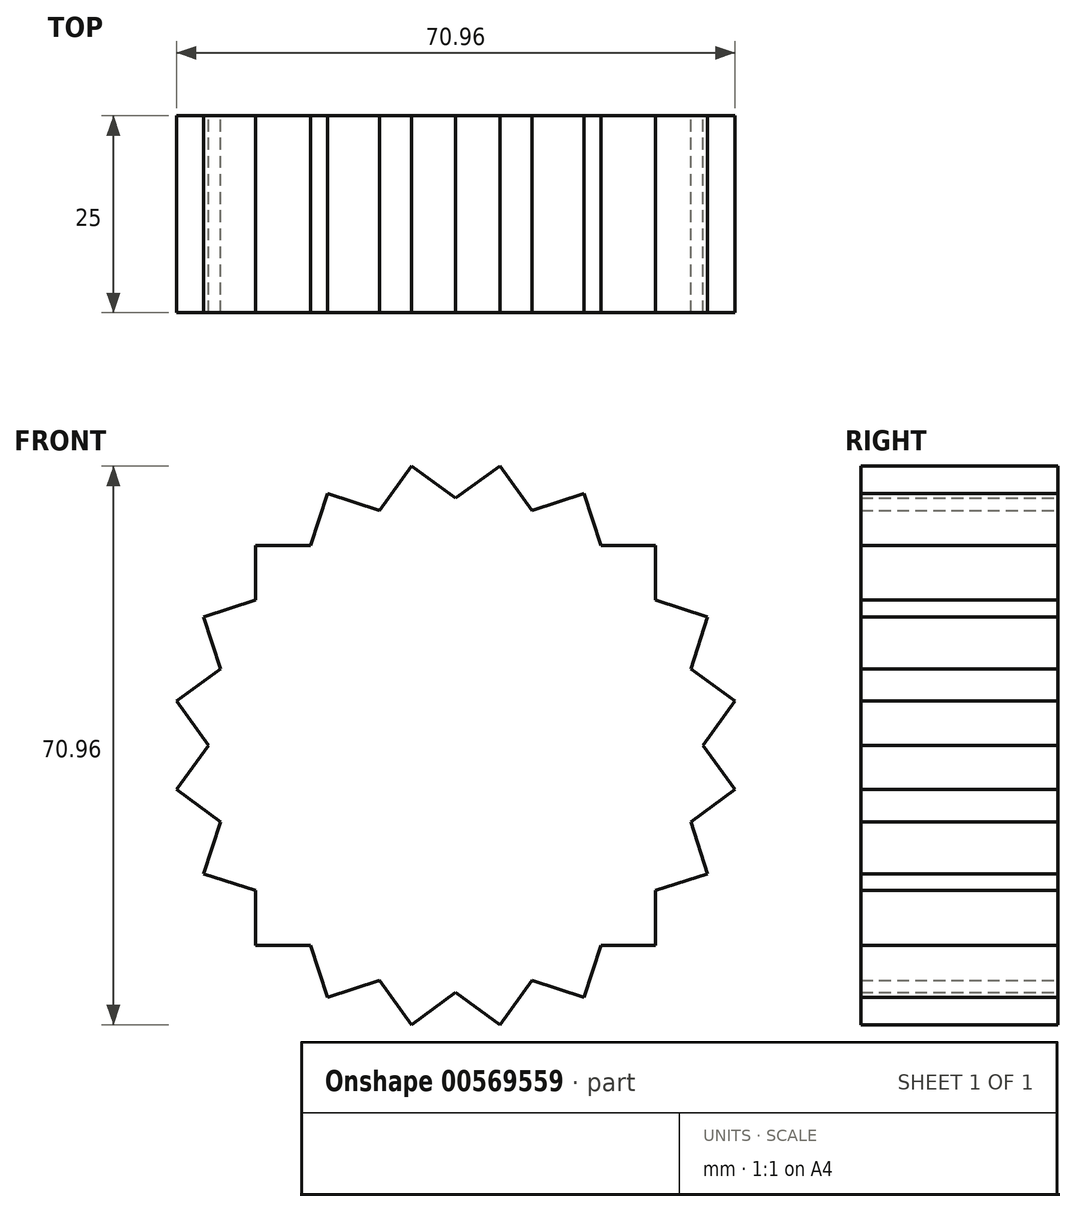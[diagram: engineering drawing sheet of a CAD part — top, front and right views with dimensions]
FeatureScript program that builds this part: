
annotation { "Feature Type Name" : "Feature", "Feature Type Description" : "" }
export const myFeature = defineFeature(function(context is Context, id is Id, definition is map)
    precondition{}
    {
        {
            var Q0;
            Q0=qCreatedBy(makeId("Front.planeOp"),FACE);
            var sketch = newSketch(context, id + "F0", { "sketchPlane" : qUnion([Q0])});
            skLineSegment(sketch, "E0.bottom", {"start": v(-25.4, 25.4) * mm, "end": v(25.4, 25.4) * mm});
            skLineSegment(sketch, "E0.top", {"start": v(-25.4, -25.4) * mm, "end": v(25.4, -25.4) * mm});
            skLineSegment(sketch, "E0.left", {"start": v(-25.4, 25.4) * mm, "end": v(-25.4, -25.4) * mm});
            skLineSegment(sketch, "E0.right", {"start": v(25.4, 25.4) * mm, "end": v(25.4, -25.4) * mm});
            skPoint(sketch, "E0.middle", {"position": v(0, 0) * mm});
            skLineSegment(sketch, "E1.1.0", {"start": v(16.3, -32) * mm, "end": v(32, 16.3) * mm});
            skLineSegment(sketch, "E1.1.1", {"start": v(-32, -16.3) * mm, "end": v(16.3, -32) * mm});
            skLineSegment(sketch, "E1.1.2", {"start": v(-32, -16.3) * mm, "end": v(-16.3, 32) * mm});
            skLineSegment(sketch, "E1.1.3", {"start": v(-16.3, 32) * mm, "end": v(32, 16.3) * mm});
            skLineSegment(sketch, "E1.2.0", {"start": v(35.48, 5.62) * mm, "end": v(-5.62, 35.48) * mm});
            skLineSegment(sketch, "E1.2.1", {"start": v(5.62, -35.48) * mm, "end": v(35.48, 5.62) * mm});
            skLineSegment(sketch, "E1.2.2", {"start": v(5.62, -35.48) * mm, "end": v(-35.48, -5.62) * mm});
            skLineSegment(sketch, "E1.2.3", {"start": v(-35.48, -5.62) * mm, "end": v(-5.62, 35.48) * mm});
            skLineSegment(sketch, "E1.3.0", {"start": v(5.62, 35.48) * mm, "end": v(-35.48, 5.62) * mm});
            skLineSegment(sketch, "E1.3.1", {"start": v(35.48, -5.62) * mm, "end": v(5.62, 35.48) * mm});
            skLineSegment(sketch, "E1.3.2", {"start": v(35.48, -5.62) * mm, "end": v(-5.62, -35.48) * mm});
            skLineSegment(sketch, "E1.3.3", {"start": v(-5.62, -35.48) * mm, "end": v(-35.48, 5.62) * mm});
            skLineSegment(sketch, "E1.4.0", {"start": v(-32, 16.3) * mm, "end": v(-16.3, -32) * mm});
            skLineSegment(sketch, "E1.4.1", {"start": v(16.3, 32) * mm, "end": v(-32, 16.3) * mm});
            skLineSegment(sketch, "E1.4.2", {"start": v(16.3, 32) * mm, "end": v(32, -16.3) * mm});
            skLineSegment(sketch, "E1.4.3", {"start": v(32, -16.3) * mm, "end": v(-16.3, -32) * mm});
            skSolve(sketch);
        }
        {
            var Q0;
            {var subQ0=sQuery(id+"F0.wireOp",EDGE,"E1.2.1");var subQ1=sQuery(id+"F0.wireOp",EDGE,"E1.1.1");var subQ2=makeQuery(id+"F0.imprint","INTERSECT",VERTEX,{"derivedFrom":[subQ1,subQ0]});Q0=makeQuery(id+"F0.imprint","IMPRINT",FACE,{"disambiguationData":[TD([[makeQuery(id+"F0.imprint","IMPRINT",EDGE,{"disambiguationData":[TD([[subQ2,1.0]])],"derivedFrom":subQ1}),-1.0]])]});}
            var Q1;
            {var subQ0=sQuery(id+"F0.wireOp",EDGE,"E1.3.0");var subQ1=sQuery(id+"F0.wireOp",EDGE,"E1.2.0");var subQ2=makeQuery(id+"F0.imprint","INTERSECT",VERTEX,{"derivedFrom":[subQ1,subQ0]});Q1=makeQuery(id+"F0.imprint","IMPRINT",FACE,{"disambiguationData":[TD([[makeQuery(id+"F0.imprint","IMPRINT",EDGE,{"disambiguationData":[TD([[subQ2,1.0]])],"derivedFrom":subQ1}),-1.0]])]});}
            var Q2;
            {var subQ0=sQuery(id+"F0.wireOp",EDGE,"E1.2.2");var subQ1=sQuery(id+"F0.wireOp",EDGE,"E1.1.2");var subQ2=makeQuery(id+"F0.imprint","INTERSECT",VERTEX,{"derivedFrom":[subQ1,subQ0]});Q2=makeQuery(id+"F0.imprint","IMPRINT",FACE,{"disambiguationData":[TD([[makeQuery(id+"F0.imprint","IMPRINT",EDGE,{"disambiguationData":[TD([[subQ2,-1.0]])],"derivedFrom":subQ1}),1.0]])]});}
            var Q3;
            {var subQ10=sQuery(id+"F0.wireOp",EDGE,"E0.bottom");var subQ24=sQuery(id+"F0.wireOp",EDGE,"E1.4.1");var subQ25=makeQuery(id+"F0.imprint","INTERSECT",VERTEX,{"derivedFrom":[subQ10,subQ24]});Q3=makeQuery(id+"F0.imprint","IMPRINT",FACE,{"disambiguationData":[TD([[makeQuery(id+"F0.imprint","IMPRINT",EDGE,{"disambiguationData":[TD([[subQ25,-1.0]])],"derivedFrom":subQ10}),-1.0]])]});}
            var Q4;
            {var subQ0=sQuery(id+"F0.wireOp",EDGE,"E1.1.3");var subQ1=sQuery(id+"F0.wireOp",EDGE,"E0.right");var subQ2=makeQuery(id+"F0.imprint","INTERSECT",VERTEX,{"derivedFrom":[subQ1,subQ0]});Q4=makeQuery(id+"F0.imprint","IMPRINT",FACE,{"disambiguationData":[TD([[makeQuery(id+"F0.imprint","IMPRINT",EDGE,{"disambiguationData":[TD([[subQ2,-1.0]])],"derivedFrom":subQ1}),-1.0]])]});}
            var Q5;
            {var subQ0=sQuery(id+"F0.wireOp",EDGE,"E1.4.0");var subQ1=sQuery(id+"F0.wireOp",EDGE,"E0.top");var subQ2=makeQuery(id+"F0.imprint","INTERSECT",VERTEX,{"derivedFrom":[subQ1,subQ0]});Q5=makeQuery(id+"F0.imprint","IMPRINT",FACE,{"disambiguationData":[TD([[makeQuery(id+"F0.imprint","IMPRINT",EDGE,{"disambiguationData":[TD([[subQ2,-1.0]])],"derivedFrom":subQ1}),1.0]])]});}
            var Q6;
            {var subQ0=sQuery(id+"F0.wireOp",EDGE,"E0.left");var subQ1=sQuery(id+"F0.wireOp",EDGE,"E0.bottom");var subQ2=makeQuery(id+"F0.imprint","INTERSECT",VERTEX,{"derivedFrom":[subQ1,subQ0]});Q6=makeQuery(id+"F0.imprint","IMPRINT",FACE,{"disambiguationData":[TD([[makeQuery(id+"F0.imprint","IMPRINT",EDGE,{"disambiguationData":[TD([[subQ2,-1.0]])],"derivedFrom":subQ1}),-1.0]])]});}
            var Q7;
            {var subQ0=sQuery(id+"F0.wireOp",EDGE,"E1.1.2");var subQ1=sQuery(id+"F0.wireOp",EDGE,"E0.bottom");var subQ2=makeQuery(id+"F0.imprint","INTERSECT",VERTEX,{"derivedFrom":[subQ1,subQ0]});Q7=makeQuery(id+"F0.imprint","IMPRINT",FACE,{"disambiguationData":[TD([[makeQuery(id+"F0.imprint","IMPRINT",EDGE,{"disambiguationData":[TD([[subQ2,-1.0]])],"derivedFrom":subQ1}),1.0]])]});}
            var Q8;
            {var subQ0=sQuery(id+"F0.wireOp",EDGE,"E1.4.2");var subQ1=sQuery(id+"F0.wireOp",EDGE,"E0.bottom");var subQ2=makeQuery(id+"F0.imprint","INTERSECT",VERTEX,{"derivedFrom":[subQ1,subQ0]});Q8=makeQuery(id+"F0.imprint","IMPRINT",FACE,{"disambiguationData":[TD([[makeQuery(id+"F0.imprint","IMPRINT",EDGE,{"disambiguationData":[TD([[subQ2,1.0]])],"derivedFrom":subQ1}),1.0]])]});}
            var Q9;
            {var subQ0=sQuery(id+"F0.wireOp",EDGE,"E0.right");var subQ1=sQuery(id+"F0.wireOp",EDGE,"E0.top");var subQ2=makeQuery(id+"F0.imprint","INTERSECT",VERTEX,{"derivedFrom":[subQ1,subQ0]});Q9=makeQuery(id+"F0.imprint","IMPRINT",FACE,{"disambiguationData":[TD([[makeQuery(id+"F0.imprint","IMPRINT",EDGE,{"disambiguationData":[TD([[subQ2,1.0]])],"derivedFrom":subQ1}),1.0]])]});}
            var Q10;
            {var subQ0=sQuery(id+"F0.wireOp",EDGE,"E1.4.1");var subQ1=sQuery(id+"F0.wireOp",EDGE,"E0.left");var subQ2=makeQuery(id+"F0.imprint","INTERSECT",VERTEX,{"derivedFrom":[subQ1,subQ0]});Q10=makeQuery(id+"F0.imprint","IMPRINT",FACE,{"disambiguationData":[TD([[makeQuery(id+"F0.imprint","IMPRINT",EDGE,{"disambiguationData":[TD([[subQ2,-1.0]])],"derivedFrom":subQ1}),-1.0]])]});}
            var Q11;
            {var subQ0=sQuery(id+"F0.wireOp",EDGE,"E1.1.3");var subQ1=sQuery(id+"F0.wireOp",EDGE,"E0.right");var subQ2=makeQuery(id+"F0.imprint","INTERSECT",VERTEX,{"derivedFrom":[subQ1,subQ0]});Q11=makeQuery(id+"F0.imprint","IMPRINT",FACE,{"disambiguationData":[TD([[makeQuery(id+"F0.imprint","IMPRINT",EDGE,{"disambiguationData":[TD([[subQ2,-1.0]])],"derivedFrom":subQ1}),1.0]])]});}
            var Q12;
            {var subQ0=sQuery(id+"F0.wireOp",EDGE,"E1.4.3");var subQ1=sQuery(id+"F0.wireOp",EDGE,"E0.right");var subQ2=makeQuery(id+"F0.imprint","INTERSECT",VERTEX,{"derivedFrom":[subQ1,subQ0]});Q12=makeQuery(id+"F0.imprint","IMPRINT",FACE,{"disambiguationData":[TD([[makeQuery(id+"F0.imprint","IMPRINT",EDGE,{"disambiguationData":[TD([[subQ2,1.0]])],"derivedFrom":subQ1}),1.0]])]});}
            var Q13;
            {var subQ0=sQuery(id+"F0.wireOp",EDGE,"E1.2.0");var subQ1=sQuery(id+"F0.wireOp",EDGE,"E1.1.0");var subQ2=makeQuery(id+"F0.imprint","INTERSECT",VERTEX,{"derivedFrom":[subQ1,subQ0]});Q13=makeQuery(id+"F0.imprint","IMPRINT",FACE,{"disambiguationData":[TD([[makeQuery(id+"F0.imprint","IMPRINT",EDGE,{"disambiguationData":[TD([[subQ2,1.0]])],"derivedFrom":subQ1}),-1.0]])]});}
            var Q14;
            {var subQ0=sQuery(id+"F0.wireOp",EDGE,"E1.2.3");var subQ1=sQuery(id+"F0.wireOp",EDGE,"E0.left");var subQ2=makeQuery(id+"F0.imprint","INTERSECT",VERTEX,{"derivedFrom":[subQ1,subQ0]});Q14=makeQuery(id+"F0.imprint","IMPRINT",FACE,{"disambiguationData":[TD([[makeQuery(id+"F0.imprint","IMPRINT",EDGE,{"disambiguationData":[TD([[subQ2,-1.0]])],"derivedFrom":subQ1}),-1.0]])]});}
            var Q15;
            {var subQ0=sQuery(id+"F0.wireOp",EDGE,"E1.3.0");var subQ1=sQuery(id+"F0.wireOp",EDGE,"E0.bottom");var subQ2=makeQuery(id+"F0.imprint","INTERSECT",VERTEX,{"derivedFrom":[subQ1,subQ0]});Q15=makeQuery(id+"F0.imprint","IMPRINT",FACE,{"disambiguationData":[TD([[makeQuery(id+"F0.imprint","IMPRINT",EDGE,{"disambiguationData":[TD([[subQ2,-1.0]])],"derivedFrom":subQ1}),1.0]])]});}
            var Q16;
            {var subQ0=sQuery(id+"F0.wireOp",EDGE,"E1.4.3");var subQ1=sQuery(id+"F0.wireOp",EDGE,"E1.1.1");var subQ2=makeQuery(id+"F0.imprint","INTERSECT",VERTEX,{"derivedFrom":[subQ1,subQ0]});Q16=makeQuery(id+"F0.imprint","IMPRINT",FACE,{"disambiguationData":[TD([[makeQuery(id+"F0.imprint","IMPRINT",EDGE,{"disambiguationData":[TD([[subQ2,-1.0]])],"derivedFrom":subQ1}),-1.0]])]});}
            var Q17;
            {var subQ0=sQuery(id+"F0.wireOp",EDGE,"E1.1.0");var subQ1=sQuery(id+"F0.wireOp",EDGE,"E0.top");var subQ2=makeQuery(id+"F0.imprint","INTERSECT",VERTEX,{"derivedFrom":[subQ1,subQ0]});Q17=makeQuery(id+"F0.imprint","IMPRINT",FACE,{"disambiguationData":[TD([[makeQuery(id+"F0.imprint","IMPRINT",EDGE,{"disambiguationData":[TD([[subQ2,1.0]])],"derivedFrom":subQ1}),1.0]])]});}
            var Q18;
            {var subQ0=sQuery(id+"F0.wireOp",EDGE,"E1.3.0");var subQ1=sQuery(id+"F0.wireOp",EDGE,"E1.1.3");var subQ2=makeQuery(id+"F0.imprint","INTERSECT",VERTEX,{"derivedFrom":[subQ1,subQ0]});Q18=makeQuery(id+"F0.imprint","IMPRINT",FACE,{"disambiguationData":[TD([[makeQuery(id+"F0.imprint","IMPRINT",EDGE,{"disambiguationData":[TD([[subQ2,-1.0]])],"derivedFrom":subQ1}),1.0]])]});}
            var Q19;
            {var subQ0=sQuery(id+"F0.wireOp",EDGE,"E1.3.3");var subQ1=sQuery(id+"F0.wireOp",EDGE,"E1.2.3");var subQ2=makeQuery(id+"F0.imprint","INTERSECT",VERTEX,{"derivedFrom":[subQ1,subQ0]});Q19=makeQuery(id+"F0.imprint","IMPRINT",FACE,{"disambiguationData":[TD([[makeQuery(id+"F0.imprint","IMPRINT",EDGE,{"disambiguationData":[TD([[subQ2,-1.0]])],"derivedFrom":subQ1}),1.0]])]});}
            var Q20;
            {var subQ0=sQuery(id+"F0.wireOp",EDGE,"E1.3.0");var subQ1=sQuery(id+"F0.wireOp",EDGE,"E1.1.2");var subQ2=makeQuery(id+"F0.imprint","INTERSECT",VERTEX,{"derivedFrom":[subQ1,subQ0]});Q20=makeQuery(id+"F0.imprint","IMPRINT",FACE,{"disambiguationData":[TD([[makeQuery(id+"F0.imprint","IMPRINT",EDGE,{"disambiguationData":[TD([[subQ2,-1.0]])],"derivedFrom":subQ1}),-1.0]])]});}
            var Q21;
            {var subQ0=sQuery(id+"F0.wireOp",EDGE,"E1.3.1");var subQ1=sQuery(id+"F0.wireOp",EDGE,"E0.right");var subQ2=makeQuery(id+"F0.imprint","INTERSECT",VERTEX,{"derivedFrom":[subQ1,subQ0]});Q21=makeQuery(id+"F0.imprint","IMPRINT",FACE,{"disambiguationData":[TD([[makeQuery(id+"F0.imprint","IMPRINT",EDGE,{"disambiguationData":[TD([[subQ2,-1.0]])],"derivedFrom":subQ1}),1.0]])]});}
            var Q22;
            {var subQ0=sQuery(id+"F0.wireOp",EDGE,"E1.2.2");var subQ1=sQuery(id+"F0.wireOp",EDGE,"E0.top");var subQ2=makeQuery(id+"F0.imprint","INTERSECT",VERTEX,{"derivedFrom":[subQ1,subQ0]});Q22=makeQuery(id+"F0.imprint","IMPRINT",FACE,{"disambiguationData":[TD([[makeQuery(id+"F0.imprint","IMPRINT",EDGE,{"disambiguationData":[TD([[subQ2,-1.0]])],"derivedFrom":subQ1}),-1.0]])]});}
            var Q23;
            {var subQ0=sQuery(id+"F0.wireOp",EDGE,"E1.1.0");var subQ1=sQuery(id+"F0.wireOp",EDGE,"E0.right");var subQ2=makeQuery(id+"F0.imprint","INTERSECT",VERTEX,{"derivedFrom":[subQ1,subQ0]});Q23=makeQuery(id+"F0.imprint","IMPRINT",FACE,{"disambiguationData":[TD([[makeQuery(id+"F0.imprint","IMPRINT",EDGE,{"disambiguationData":[TD([[subQ2,-1.0]])],"derivedFrom":subQ1}),1.0]])]});}
            var Q24;
            {var subQ0=sQuery(id+"F0.wireOp",EDGE,"E1.3.3");var subQ1=sQuery(id+"F0.wireOp",EDGE,"E0.left");var subQ2=makeQuery(id+"F0.imprint","INTERSECT",VERTEX,{"derivedFrom":[subQ1,subQ0]});Q24=makeQuery(id+"F0.imprint","IMPRINT",FACE,{"disambiguationData":[TD([[makeQuery(id+"F0.imprint","IMPRINT",EDGE,{"disambiguationData":[TD([[subQ2,-1.0]])],"derivedFrom":subQ1}),-1.0]])]});}
            var Q25;
            {var subQ0=sQuery(id+"F0.wireOp",EDGE,"E1.2.1");var subQ1=sQuery(id+"F0.wireOp",EDGE,"E0.right");var subQ2=makeQuery(id+"F0.imprint","INTERSECT",VERTEX,{"derivedFrom":[subQ1,subQ0]});Q25=makeQuery(id+"F0.imprint","IMPRINT",FACE,{"disambiguationData":[TD([[makeQuery(id+"F0.imprint","IMPRINT",EDGE,{"disambiguationData":[TD([[subQ2,-1.0]])],"derivedFrom":subQ1}),1.0]])]});}
            var Q26;
            {var subQ0=sQuery(id+"F0.wireOp",EDGE,"E1.3.0");var subQ1=sQuery(id+"F0.wireOp",EDGE,"E0.left");var subQ2=makeQuery(id+"F0.imprint","INTERSECT",VERTEX,{"derivedFrom":[subQ1,subQ0]});Q26=makeQuery(id+"F0.imprint","IMPRINT",FACE,{"disambiguationData":[TD([[makeQuery(id+"F0.imprint","IMPRINT",EDGE,{"disambiguationData":[TD([[subQ2,-1.0]])],"derivedFrom":subQ1}),-1.0]])]});}
            var Q27;
            {var subQ0=sQuery(id+"F0.wireOp",EDGE,"E1.3.2");var subQ1=sQuery(id+"F0.wireOp",EDGE,"E0.top");var subQ2=makeQuery(id+"F0.imprint","INTERSECT",VERTEX,{"derivedFrom":[subQ1,subQ0]});Q27=makeQuery(id+"F0.imprint","IMPRINT",FACE,{"disambiguationData":[TD([[makeQuery(id+"F0.imprint","IMPRINT",EDGE,{"disambiguationData":[TD([[subQ2,-1.0]])],"derivedFrom":subQ1}),1.0]])]});}
            var Q28;
            {var subQ0=sQuery(id+"F0.wireOp",EDGE,"E0.right");var subQ1=sQuery(id+"F0.wireOp",EDGE,"E0.bottom");var subQ2=makeQuery(id+"F0.imprint","INTERSECT",VERTEX,{"derivedFrom":[subQ1,subQ0]});Q28=makeQuery(id+"F0.imprint","IMPRINT",FACE,{"disambiguationData":[TD([[makeQuery(id+"F0.imprint","IMPRINT",EDGE,{"disambiguationData":[TD([[subQ2,1.0]])],"derivedFrom":subQ1}),-1.0]])]});}
            var Q29;
            {var subQ0=sQuery(id+"F0.wireOp",EDGE,"E1.2.0");var subQ1=sQuery(id+"F0.wireOp",EDGE,"E0.bottom");var subQ2=makeQuery(id+"F0.imprint","INTERSECT",VERTEX,{"derivedFrom":[subQ1,subQ0]});Q29=makeQuery(id+"F0.imprint","IMPRINT",FACE,{"disambiguationData":[TD([[makeQuery(id+"F0.imprint","IMPRINT",EDGE,{"disambiguationData":[TD([[subQ2,-1.0]])],"derivedFrom":subQ1}),-1.0]])]});}
            var Q30;
            {var subQ0=sQuery(id+"F0.wireOp",EDGE,"E1.4.3");var subQ1=sQuery(id+"F0.wireOp",EDGE,"E0.top");var subQ2=makeQuery(id+"F0.imprint","INTERSECT",VERTEX,{"derivedFrom":[subQ1,subQ0]});Q30=makeQuery(id+"F0.imprint","IMPRINT",FACE,{"disambiguationData":[TD([[makeQuery(id+"F0.imprint","IMPRINT",EDGE,{"disambiguationData":[TD([[subQ2,-1.0]])],"derivedFrom":subQ1}),-1.0]])]});}
            var Q31;
            {var subQ0=sQuery(id+"F0.wireOp",EDGE,"E0.left");var subQ1=sQuery(id+"F0.wireOp",EDGE,"E0.top");var subQ2=makeQuery(id+"F0.imprint","INTERSECT",VERTEX,{"derivedFrom":[subQ1,subQ0]});Q31=makeQuery(id+"F0.imprint","IMPRINT",FACE,{"disambiguationData":[TD([[makeQuery(id+"F0.imprint","IMPRINT",EDGE,{"disambiguationData":[TD([[subQ2,-1.0]])],"derivedFrom":subQ1}),1.0]])]});}
            var Q32;
            {var subQ0=sQuery(id+"F0.wireOp",EDGE,"E1.4.0");var subQ1=sQuery(id+"F0.wireOp",EDGE,"E0.top");var subQ2=makeQuery(id+"F0.imprint","INTERSECT",VERTEX,{"derivedFrom":[subQ1,subQ0]});Q32=makeQuery(id+"F0.imprint","IMPRINT",FACE,{"disambiguationData":[TD([[makeQuery(id+"F0.imprint","IMPRINT",EDGE,{"disambiguationData":[TD([[subQ2,-1.0]])],"derivedFrom":subQ1}),-1.0]])]});}
            var Q33;
            {var subQ0=sQuery(id+"F0.wireOp",EDGE,"E1.1.0");var subQ1=sQuery(id+"F0.wireOp",EDGE,"E0.top");var subQ2=makeQuery(id+"F0.imprint","INTERSECT",VERTEX,{"derivedFrom":[subQ1,subQ0]});Q33=makeQuery(id+"F0.imprint","IMPRINT",FACE,{"disambiguationData":[TD([[makeQuery(id+"F0.imprint","IMPRINT",EDGE,{"disambiguationData":[TD([[subQ2,1.0]])],"derivedFrom":subQ1}),-1.0]])]});}
            var Q34;
            {var subQ0=sQuery(id+"F0.wireOp",EDGE,"E1.1.1");var subQ1=sQuery(id+"F0.wireOp",EDGE,"E0.left");var subQ2=makeQuery(id+"F0.imprint","INTERSECT",VERTEX,{"derivedFrom":[subQ1,subQ0]});Q34=makeQuery(id+"F0.imprint","IMPRINT",FACE,{"disambiguationData":[TD([[makeQuery(id+"F0.imprint","IMPRINT",EDGE,{"disambiguationData":[TD([[subQ2,1.0]])],"derivedFrom":subQ1}),-1.0]])]});}
            var Q35;
            {var subQ0=sQuery(id+"F0.wireOp",EDGE,"E1.4.3");var subQ1=sQuery(id+"F0.wireOp",EDGE,"E0.right");var subQ2=makeQuery(id+"F0.imprint","INTERSECT",VERTEX,{"derivedFrom":[subQ1,subQ0]});Q35=makeQuery(id+"F0.imprint","IMPRINT",FACE,{"disambiguationData":[TD([[makeQuery(id+"F0.imprint","IMPRINT",EDGE,{"disambiguationData":[TD([[subQ2,1.0]])],"derivedFrom":subQ1}),-1.0]])]});}
            var Q36;
            {var subQ0=sQuery(id+"F0.wireOp",EDGE,"E1.2.1");var subQ1=sQuery(id+"F0.wireOp",EDGE,"E0.right");var subQ2=makeQuery(id+"F0.imprint","INTERSECT",VERTEX,{"derivedFrom":[subQ1,subQ0]});Q36=makeQuery(id+"F0.imprint","IMPRINT",FACE,{"disambiguationData":[TD([[makeQuery(id+"F0.imprint","IMPRINT",EDGE,{"disambiguationData":[TD([[subQ2,-1.0]])],"derivedFrom":subQ1}),-1.0]])]});}
            var Q37;
            {var subQ0=sQuery(id+"F0.wireOp",EDGE,"E1.3.3");var subQ1=sQuery(id+"F0.wireOp",EDGE,"E0.left");var subQ2=makeQuery(id+"F0.imprint","INTERSECT",VERTEX,{"derivedFrom":[subQ1,subQ0]});Q37=makeQuery(id+"F0.imprint","IMPRINT",FACE,{"disambiguationData":[TD([[makeQuery(id+"F0.imprint","IMPRINT",EDGE,{"disambiguationData":[TD([[subQ2,-1.0]])],"derivedFrom":subQ1}),1.0]])]});}
            var Q38;
            {var subQ0=sQuery(id+"F0.wireOp",EDGE,"E1.2.3");var subQ1=sQuery(id+"F0.wireOp",EDGE,"E1.1.3");var subQ2=makeQuery(id+"F0.imprint","INTERSECT",VERTEX,{"derivedFrom":[subQ1,subQ0]});Q38=makeQuery(id+"F0.imprint","IMPRINT",FACE,{"disambiguationData":[TD([[makeQuery(id+"F0.imprint","IMPRINT",EDGE,{"disambiguationData":[TD([[subQ2,-1.0]])],"derivedFrom":subQ1}),1.0]])]});}
            var Q39;
            {var subQ0=sQuery(id+"F0.wireOp",EDGE,"E1.3.2");var subQ1=sQuery(id+"F0.wireOp",EDGE,"E0.top");var subQ2=makeQuery(id+"F0.imprint","INTERSECT",VERTEX,{"derivedFrom":[subQ1,subQ0]});Q39=makeQuery(id+"F0.imprint","IMPRINT",FACE,{"disambiguationData":[TD([[makeQuery(id+"F0.imprint","IMPRINT",EDGE,{"disambiguationData":[TD([[subQ2,-1.0]])],"derivedFrom":subQ1}),-1.0]])]});}
            var Q40;
            {var subQ0=sQuery(id+"F0.wireOp",EDGE,"E1.2.0");var subQ1=sQuery(id+"F0.wireOp",EDGE,"E0.bottom");var subQ2=makeQuery(id+"F0.imprint","INTERSECT",VERTEX,{"derivedFrom":[subQ1,subQ0]});Q40=makeQuery(id+"F0.imprint","IMPRINT",FACE,{"disambiguationData":[TD([[makeQuery(id+"F0.imprint","IMPRINT",EDGE,{"disambiguationData":[TD([[subQ2,-1.0]])],"derivedFrom":subQ1}),1.0]])]});}
            var Q41;
            {var subQ0=sQuery(id+"F0.wireOp",EDGE,"E1.4.2");var subQ1=sQuery(id+"F0.wireOp",EDGE,"E0.bottom");var subQ2=makeQuery(id+"F0.imprint","INTERSECT",VERTEX,{"derivedFrom":[subQ1,subQ0]});Q41=makeQuery(id+"F0.imprint","IMPRINT",FACE,{"disambiguationData":[TD([[makeQuery(id+"F0.imprint","IMPRINT",EDGE,{"disambiguationData":[TD([[subQ2,1.0]])],"derivedFrom":subQ1}),-1.0]])]});}
            var Q42;
            {var subQ0=sQuery(id+"F0.wireOp",EDGE,"E1.3.1");var subQ1=sQuery(id+"F0.wireOp",EDGE,"E1.2.1");var subQ2=makeQuery(id+"F0.imprint","INTERSECT",VERTEX,{"derivedFrom":[subQ1,subQ0]});Q42=makeQuery(id+"F0.imprint","IMPRINT",FACE,{"disambiguationData":[TD([[makeQuery(id+"F0.imprint","IMPRINT",EDGE,{"disambiguationData":[TD([[subQ2,1.0]])],"derivedFrom":subQ1}),-1.0]])]});}
            var Q43;
            {var subQ0=sQuery(id+"F0.wireOp",EDGE,"E1.4.2");var subQ1=sQuery(id+"F0.wireOp",EDGE,"E1.1.0");var subQ2=makeQuery(id+"F0.imprint","INTERSECT",VERTEX,{"derivedFrom":[subQ1,subQ0]});Q43=makeQuery(id+"F0.imprint","IMPRINT",FACE,{"disambiguationData":[TD([[makeQuery(id+"F0.imprint","IMPRINT",EDGE,{"disambiguationData":[TD([[subQ2,-1.0]])],"derivedFrom":subQ1}),-1.0]])]});}
            var Q44;
            {var subQ0=sQuery(id+"F0.wireOp",EDGE,"E1.3.1");var subQ1=sQuery(id+"F0.wireOp",EDGE,"E1.1.3");var subQ2=makeQuery(id+"F0.imprint","INTERSECT",VERTEX,{"derivedFrom":[subQ1,subQ0]});Q44=makeQuery(id+"F0.imprint","IMPRINT",FACE,{"disambiguationData":[TD([[makeQuery(id+"F0.imprint","IMPRINT",EDGE,{"disambiguationData":[TD([[subQ2,-1.0]])],"derivedFrom":subQ1}),-1.0]])]});}
            var Q45;
            {var subQ0=sQuery(id+"F0.wireOp",EDGE,"E1.1.1");var subQ1=sQuery(id+"F0.wireOp",EDGE,"E0.left");var subQ2=makeQuery(id+"F0.imprint","INTERSECT",VERTEX,{"derivedFrom":[subQ1,subQ0]});Q45=makeQuery(id+"F0.imprint","IMPRINT",FACE,{"disambiguationData":[TD([[makeQuery(id+"F0.imprint","IMPRINT",EDGE,{"disambiguationData":[TD([[subQ2,1.0]])],"derivedFrom":subQ1}),1.0]])]});}
            var Q46;
            {var subQ0=sQuery(id+"F0.wireOp",EDGE,"E1.3.0");var subQ1=sQuery(id+"F0.wireOp",EDGE,"E0.left");var subQ2=makeQuery(id+"F0.imprint","INTERSECT",VERTEX,{"derivedFrom":[subQ1,subQ0]});Q46=makeQuery(id+"F0.imprint","IMPRINT",FACE,{"disambiguationData":[TD([[makeQuery(id+"F0.imprint","IMPRINT",EDGE,{"disambiguationData":[TD([[subQ2,-1.0]])],"derivedFrom":subQ1}),1.0]])]});}
            var Q47;
            {var subQ0=sQuery(id+"F0.wireOp",EDGE,"E1.2.3");var subQ1=sQuery(id+"F0.wireOp",EDGE,"E0.bottom");var subQ2=makeQuery(id+"F0.imprint","INTERSECT",VERTEX,{"derivedFrom":[subQ1,subQ0]});Q47=makeQuery(id+"F0.imprint","IMPRINT",FACE,{"disambiguationData":[TD([[makeQuery(id+"F0.imprint","IMPRINT",EDGE,{"disambiguationData":[TD([[subQ2,-1.0]])],"derivedFrom":subQ1}),1.0]])]});}
            var Q48;
            {var subQ0=sQuery(id+"F0.wireOp",EDGE,"E1.4.3");var subQ1=sQuery(id+"F0.wireOp",EDGE,"E1.1.0");var subQ2=makeQuery(id+"F0.imprint","INTERSECT",VERTEX,{"derivedFrom":[subQ1,subQ0]});Q48=makeQuery(id+"F0.imprint","IMPRINT",FACE,{"disambiguationData":[TD([[makeQuery(id+"F0.imprint","IMPRINT",EDGE,{"disambiguationData":[TD([[subQ2,-1.0]])],"derivedFrom":subQ1}),1.0]])]});}
            var Q49;
            {var subQ0=sQuery(id+"F0.wireOp",EDGE,"E1.4.1");var subQ1=sQuery(id+"F0.wireOp",EDGE,"E0.left");var subQ2=makeQuery(id+"F0.imprint","INTERSECT",VERTEX,{"derivedFrom":[subQ1,subQ0]});Q49=makeQuery(id+"F0.imprint","IMPRINT",FACE,{"disambiguationData":[TD([[makeQuery(id+"F0.imprint","IMPRINT",EDGE,{"disambiguationData":[TD([[subQ2,-1.0]])],"derivedFrom":subQ1}),1.0]])]});}
            var Q50;
            {var subQ0=sQuery(id+"F0.wireOp",EDGE,"E1.3.3");var subQ1=sQuery(id+"F0.wireOp",EDGE,"E1.1.2");var subQ2=makeQuery(id+"F0.imprint","INTERSECT",VERTEX,{"derivedFrom":[subQ1,subQ0]});Q50=makeQuery(id+"F0.imprint","IMPRINT",FACE,{"disambiguationData":[TD([[makeQuery(id+"F0.imprint","IMPRINT",EDGE,{"disambiguationData":[TD([[subQ2,-1.0]])],"derivedFrom":subQ1}),1.0]])]});}
            var Q51;
            {var subQ0=sQuery(id+"F0.wireOp",EDGE,"E1.2.0");var subQ1=sQuery(id+"F0.wireOp",EDGE,"E0.right");var subQ2=makeQuery(id+"F0.imprint","INTERSECT",VERTEX,{"derivedFrom":[subQ1,subQ0]});Q51=makeQuery(id+"F0.imprint","IMPRINT",FACE,{"disambiguationData":[TD([[makeQuery(id+"F0.imprint","IMPRINT",EDGE,{"disambiguationData":[TD([[subQ2,-1.0]])],"derivedFrom":subQ1}),-1.0]])]});}
            var Q52;
            {var subQ0=sQuery(id+"F0.wireOp",EDGE,"E1.3.3");var subQ1=sQuery(id+"F0.wireOp",EDGE,"E0.top");var subQ2=makeQuery(id+"F0.imprint","INTERSECT",VERTEX,{"derivedFrom":[subQ1,subQ0]});Q52=makeQuery(id+"F0.imprint","IMPRINT",FACE,{"disambiguationData":[TD([[makeQuery(id+"F0.imprint","IMPRINT",EDGE,{"disambiguationData":[TD([[subQ2,-1.0]])],"derivedFrom":subQ1}),-1.0]])]});}
            var Q53;
            {var subQ0=sQuery(id+"F0.wireOp",EDGE,"E1.2.0");var subQ1=sQuery(id+"F0.wireOp",EDGE,"E0.right");var subQ2=makeQuery(id+"F0.imprint","INTERSECT",VERTEX,{"derivedFrom":[subQ1,subQ0]});Q53=makeQuery(id+"F0.imprint","IMPRINT",FACE,{"disambiguationData":[TD([[makeQuery(id+"F0.imprint","IMPRINT",EDGE,{"disambiguationData":[TD([[subQ2,-1.0]])],"derivedFrom":subQ1}),1.0]])]});}
            var Q54;
            {var subQ0=sQuery(id+"F0.wireOp",EDGE,"E1.3.3");var subQ1=sQuery(id+"F0.wireOp",EDGE,"E0.top");var subQ2=makeQuery(id+"F0.imprint","INTERSECT",VERTEX,{"derivedFrom":[subQ1,subQ0]});Q54=makeQuery(id+"F0.imprint","IMPRINT",FACE,{"disambiguationData":[TD([[makeQuery(id+"F0.imprint","IMPRINT",EDGE,{"disambiguationData":[TD([[subQ2,-1.0]])],"derivedFrom":subQ1}),1.0]])]});}
            var Q55;
            {var subQ0=sQuery(id+"F0.wireOp",EDGE,"E1.4.0");var subQ1=sQuery(id+"F0.wireOp",EDGE,"E0.left");var subQ2=makeQuery(id+"F0.imprint","INTERSECT",VERTEX,{"derivedFrom":[subQ1,subQ0]});Q55=makeQuery(id+"F0.imprint","IMPRINT",FACE,{"disambiguationData":[TD([[makeQuery(id+"F0.imprint","IMPRINT",EDGE,{"disambiguationData":[TD([[subQ2,-1.0]])],"derivedFrom":subQ1}),-1.0]])]});}
            var Q56;
            {var subQ0=sQuery(id+"F0.wireOp",EDGE,"E1.1.3");var subQ1=sQuery(id+"F0.wireOp",EDGE,"E0.bottom");var subQ2=makeQuery(id+"F0.imprint","INTERSECT",VERTEX,{"derivedFrom":[subQ1,subQ0]});Q56=makeQuery(id+"F0.imprint","IMPRINT",FACE,{"disambiguationData":[TD([[makeQuery(id+"F0.imprint","IMPRINT",EDGE,{"disambiguationData":[TD([[subQ2,-1.0]])],"derivedFrom":subQ1}),1.0]])]});}
            var Q57;
            {var subQ0=sQuery(id+"F0.wireOp",EDGE,"E1.1.2");var subQ1=sQuery(id+"F0.wireOp",EDGE,"E0.bottom");var subQ2=makeQuery(id+"F0.imprint","INTERSECT",VERTEX,{"derivedFrom":[subQ1,subQ0]});Q57=makeQuery(id+"F0.imprint","IMPRINT",FACE,{"disambiguationData":[TD([[makeQuery(id+"F0.imprint","IMPRINT",EDGE,{"disambiguationData":[TD([[subQ2,-1.0]])],"derivedFrom":subQ1}),-1.0]])]});}
            var Q58;
            {var subQ0=sQuery(id+"F0.wireOp",EDGE,"E1.3.2");var subQ1=sQuery(id+"F0.wireOp",EDGE,"E1.2.2");var subQ2=makeQuery(id+"F0.imprint","INTERSECT",VERTEX,{"derivedFrom":[subQ1,subQ0]});Q58=makeQuery(id+"F0.imprint","IMPRINT",FACE,{"disambiguationData":[TD([[makeQuery(id+"F0.imprint","IMPRINT",EDGE,{"disambiguationData":[TD([[subQ2,-1.0]])],"derivedFrom":subQ1}),1.0]])]});}
            var Q59;
            {var subQ0=sQuery(id+"F0.wireOp",EDGE,"E1.4.0");var subQ1=sQuery(id+"F0.wireOp",EDGE,"E1.1.1");var subQ2=makeQuery(id+"F0.imprint","INTERSECT",VERTEX,{"derivedFrom":[subQ1,subQ0]});Q59=makeQuery(id+"F0.imprint","IMPRINT",FACE,{"disambiguationData":[TD([[makeQuery(id+"F0.imprint","IMPRINT",EDGE,{"disambiguationData":[TD([[subQ2,-1.0]])],"derivedFrom":subQ1}),1.0]])]});}
            var Q60;
            {var subQ0=sQuery(id+"F0.wireOp",EDGE,"E1.2.3");var subQ1=sQuery(id+"F0.wireOp",EDGE,"E0.bottom");var subQ2=makeQuery(id+"F0.imprint","INTERSECT",VERTEX,{"derivedFrom":[subQ1,subQ0]});Q60=makeQuery(id+"F0.imprint","IMPRINT",FACE,{"disambiguationData":[TD([[makeQuery(id+"F0.imprint","IMPRINT",EDGE,{"disambiguationData":[TD([[subQ2,-1.0]])],"derivedFrom":subQ1}),-1.0]])]});}
            var Q61;
            {var subQ0=sQuery(id+"F0.wireOp",EDGE,"E1.3.2");var subQ1=sQuery(id+"F0.wireOp",EDGE,"E1.1.0");var subQ2=makeQuery(id+"F0.imprint","INTERSECT",VERTEX,{"derivedFrom":[subQ1,subQ0]});Q61=makeQuery(id+"F0.imprint","IMPRINT",FACE,{"disambiguationData":[TD([[makeQuery(id+"F0.imprint","IMPRINT",EDGE,{"disambiguationData":[TD([[subQ2,-1.0]])],"derivedFrom":subQ1}),1.0]])]});}
            var Q62;
            {var subQ0=sQuery(id+"F0.wireOp",EDGE,"E1.1.2");var subQ1=sQuery(id+"F0.wireOp",EDGE,"E0.left");var subQ2=makeQuery(id+"F0.imprint","INTERSECT",VERTEX,{"derivedFrom":[subQ1,subQ0]});Q62=makeQuery(id+"F0.imprint","IMPRINT",FACE,{"disambiguationData":[TD([[makeQuery(id+"F0.imprint","IMPRINT",EDGE,{"disambiguationData":[TD([[subQ2,-1.0]])],"derivedFrom":subQ1}),-1.0]])]});}
            var Q63;
            {var subQ0=sQuery(id+"F0.wireOp",EDGE,"E1.2.0");var subQ1=sQuery(id+"F0.wireOp",EDGE,"E1.1.3");var subQ2=makeQuery(id+"F0.imprint","INTERSECT",VERTEX,{"derivedFrom":[subQ1,subQ0]});Q63=makeQuery(id+"F0.imprint","IMPRINT",FACE,{"disambiguationData":[TD([[makeQuery(id+"F0.imprint","IMPRINT",EDGE,{"disambiguationData":[TD([[subQ2,-1.0]])],"derivedFrom":subQ1}),-1.0]])]});}
            var Q64;
            {var subQ0=sQuery(id+"F0.wireOp",EDGE,"E1.4.2");var subQ1=sQuery(id+"F0.wireOp",EDGE,"E1.2.0");var subQ2=makeQuery(id+"F0.imprint","INTERSECT",VERTEX,{"derivedFrom":[subQ1,subQ0]});Q64=makeQuery(id+"F0.imprint","IMPRINT",FACE,{"disambiguationData":[TD([[makeQuery(id+"F0.imprint","IMPRINT",EDGE,{"disambiguationData":[TD([[subQ2,-1.0]])],"derivedFrom":subQ1}),1.0]])]});}
            var Q65;
            {var subQ0=sQuery(id+"F0.wireOp",EDGE,"E1.3.1");var subQ1=sQuery(id+"F0.wireOp",EDGE,"E0.right");var subQ2=makeQuery(id+"F0.imprint","INTERSECT",VERTEX,{"derivedFrom":[subQ1,subQ0]});Q65=makeQuery(id+"F0.imprint","IMPRINT",FACE,{"disambiguationData":[TD([[makeQuery(id+"F0.imprint","IMPRINT",EDGE,{"disambiguationData":[TD([[subQ2,-1.0]])],"derivedFrom":subQ1}),-1.0]])]});}
            var Q66;
            {var subQ0=sQuery(id+"F0.wireOp",EDGE,"E1.3.0");var subQ1=sQuery(id+"F0.wireOp",EDGE,"E1.2.3");var subQ2=makeQuery(id+"F0.imprint","INTERSECT",VERTEX,{"derivedFrom":[subQ1,subQ0]});Q66=makeQuery(id+"F0.imprint","IMPRINT",FACE,{"disambiguationData":[TD([[makeQuery(id+"F0.imprint","IMPRINT",EDGE,{"disambiguationData":[TD([[subQ2,-1.0]])],"derivedFrom":subQ1}),-1.0]])]});}
            var Q67;
            {var subQ0=sQuery(id+"F0.wireOp",EDGE,"E1.2.2");var subQ1=sQuery(id+"F0.wireOp",EDGE,"E0.top");var subQ2=makeQuery(id+"F0.imprint","INTERSECT",VERTEX,{"derivedFrom":[subQ1,subQ0]});Q67=makeQuery(id+"F0.imprint","IMPRINT",FACE,{"disambiguationData":[TD([[makeQuery(id+"F0.imprint","IMPRINT",EDGE,{"disambiguationData":[TD([[subQ2,-1.0]])],"derivedFrom":subQ1}),1.0]])]});}
            var Q68;
            {var subQ0=sQuery(id+"F0.wireOp",EDGE,"E1.4.1");var subQ1=sQuery(id+"F0.wireOp",EDGE,"E0.bottom");var subQ2=makeQuery(id+"F0.imprint","INTERSECT",VERTEX,{"derivedFrom":[subQ1,subQ0]});Q68=makeQuery(id+"F0.imprint","IMPRINT",FACE,{"disambiguationData":[TD([[makeQuery(id+"F0.imprint","IMPRINT",EDGE,{"disambiguationData":[TD([[subQ2,-1.0]])],"derivedFrom":subQ1}),1.0]])]});}
            var Q69;
            {var subQ0=sQuery(id+"F0.wireOp",EDGE,"E1.4.3");var subQ1=sQuery(id+"F0.wireOp",EDGE,"E1.2.1");var subQ2=makeQuery(id+"F0.imprint","INTERSECT",VERTEX,{"derivedFrom":[subQ1,subQ0]});Q69=makeQuery(id+"F0.imprint","IMPRINT",FACE,{"disambiguationData":[TD([[makeQuery(id+"F0.imprint","IMPRINT",EDGE,{"disambiguationData":[TD([[subQ2,-1.0]])],"derivedFrom":subQ1}),1.0]])]});}
            var Q70;
            {var subQ0=sQuery(id+"F0.wireOp",EDGE,"E1.1.1");var subQ1=sQuery(id+"F0.wireOp",EDGE,"E0.top");var subQ2=makeQuery(id+"F0.imprint","INTERSECT",VERTEX,{"derivedFrom":[subQ1,subQ0]});Q70=makeQuery(id+"F0.imprint","IMPRINT",FACE,{"disambiguationData":[TD([[makeQuery(id+"F0.imprint","IMPRINT",EDGE,{"disambiguationData":[TD([[subQ2,-1.0]])],"derivedFrom":subQ1}),-1.0]])]});}
            var Q71;
            {var subQ0=sQuery(id+"F0.wireOp",EDGE,"E1.4.3");var subQ1=sQuery(id+"F0.wireOp",EDGE,"E0.top");var subQ2=makeQuery(id+"F0.imprint","INTERSECT",VERTEX,{"derivedFrom":[subQ1,subQ0]});Q71=makeQuery(id+"F0.imprint","IMPRINT",FACE,{"disambiguationData":[TD([[makeQuery(id+"F0.imprint","IMPRINT",EDGE,{"disambiguationData":[TD([[subQ2,-1.0]])],"derivedFrom":subQ1}),1.0]])]});}
            var Q72;
            {var subQ0=sQuery(id+"F0.wireOp",EDGE,"E1.3.3");var subQ1=sQuery(id+"F0.wireOp",EDGE,"E1.1.1");var subQ2=makeQuery(id+"F0.imprint","INTERSECT",VERTEX,{"derivedFrom":[subQ1,subQ0]});Q72=makeQuery(id+"F0.imprint","IMPRINT",FACE,{"disambiguationData":[TD([[makeQuery(id+"F0.imprint","IMPRINT",EDGE,{"disambiguationData":[TD([[subQ2,-1.0]])],"derivedFrom":subQ1}),1.0]])]});}
            var Q73;
            {var subQ0=sQuery(id+"F0.wireOp",EDGE,"E1.2.3");var subQ1=sQuery(id+"F0.wireOp",EDGE,"E1.1.2");var subQ2=makeQuery(id+"F0.imprint","INTERSECT",VERTEX,{"derivedFrom":[subQ1,subQ0]});Q73=makeQuery(id+"F0.imprint","IMPRINT",FACE,{"disambiguationData":[TD([[makeQuery(id+"F0.imprint","IMPRINT",EDGE,{"disambiguationData":[TD([[subQ2,-1.0]])],"derivedFrom":subQ1}),-1.0]])]});}
            var Q74;
            {var subQ0=sQuery(id+"F0.wireOp",EDGE,"E1.1.0");var subQ1=sQuery(id+"F0.wireOp",EDGE,"E0.right");var subQ2=makeQuery(id+"F0.imprint","INTERSECT",VERTEX,{"derivedFrom":[subQ1,subQ0]});Q74=makeQuery(id+"F0.imprint","IMPRINT",FACE,{"disambiguationData":[TD([[makeQuery(id+"F0.imprint","IMPRINT",EDGE,{"disambiguationData":[TD([[subQ2,-1.0]])],"derivedFrom":subQ1}),-1.0]])]});}
            var Q75;
            {var subQ0=sQuery(id+"F0.wireOp",EDGE,"E1.4.0");var subQ1=sQuery(id+"F0.wireOp",EDGE,"E0.left");var subQ2=makeQuery(id+"F0.imprint","INTERSECT",VERTEX,{"derivedFrom":[subQ1,subQ0]});Q75=makeQuery(id+"F0.imprint","IMPRINT",FACE,{"disambiguationData":[TD([[makeQuery(id+"F0.imprint","IMPRINT",EDGE,{"disambiguationData":[TD([[subQ2,-1.0]])],"derivedFrom":subQ1}),1.0]])]});}
            var Q76;
            {var subQ0=sQuery(id+"F0.wireOp",EDGE,"E1.4.2");var subQ1=sQuery(id+"F0.wireOp",EDGE,"E0.right");var subQ2=makeQuery(id+"F0.imprint","INTERSECT",VERTEX,{"derivedFrom":[subQ1,subQ0]});Q76=makeQuery(id+"F0.imprint","IMPRINT",FACE,{"disambiguationData":[TD([[makeQuery(id+"F0.imprint","IMPRINT",EDGE,{"disambiguationData":[TD([[subQ2,-1.0]])],"derivedFrom":subQ1}),1.0]])]});}
            var Q77;
            {var subQ0=sQuery(id+"F0.wireOp",EDGE,"E1.3.0");var subQ1=sQuery(id+"F0.wireOp",EDGE,"E0.bottom");var subQ2=makeQuery(id+"F0.imprint","INTERSECT",VERTEX,{"derivedFrom":[subQ1,subQ0]});Q77=makeQuery(id+"F0.imprint","IMPRINT",FACE,{"disambiguationData":[TD([[makeQuery(id+"F0.imprint","IMPRINT",EDGE,{"disambiguationData":[TD([[subQ2,-1.0]])],"derivedFrom":subQ1}),-1.0]])]});}
            var Q78;
            {var subQ0=sQuery(id+"F0.wireOp",EDGE,"E1.1.3");var subQ1=sQuery(id+"F0.wireOp",EDGE,"E0.bottom");var subQ2=makeQuery(id+"F0.imprint","INTERSECT",VERTEX,{"derivedFrom":[subQ1,subQ0]});Q78=makeQuery(id+"F0.imprint","IMPRINT",FACE,{"disambiguationData":[TD([[makeQuery(id+"F0.imprint","IMPRINT",EDGE,{"disambiguationData":[TD([[subQ2,-1.0]])],"derivedFrom":subQ1}),-1.0]])]});}
            var Q79;
            {var subQ0=sQuery(id+"F0.wireOp",EDGE,"E1.3.3");var subQ1=sQuery(id+"F0.wireOp",EDGE,"E1.2.2");var subQ2=makeQuery(id+"F0.imprint","INTERSECT",VERTEX,{"derivedFrom":[subQ1,subQ0]});Q79=makeQuery(id+"F0.imprint","IMPRINT",FACE,{"disambiguationData":[TD([[makeQuery(id+"F0.imprint","IMPRINT",EDGE,{"disambiguationData":[TD([[subQ2,-1.0]])],"derivedFrom":subQ1}),-1.0]])]});}
            var Q80;
            {var subQ0=sQuery(id+"F0.wireOp",EDGE,"E1.2.3");var subQ1=sQuery(id+"F0.wireOp",EDGE,"E0.left");var subQ2=makeQuery(id+"F0.imprint","INTERSECT",VERTEX,{"derivedFrom":[subQ1,subQ0]});Q80=makeQuery(id+"F0.imprint","IMPRINT",FACE,{"disambiguationData":[TD([[makeQuery(id+"F0.imprint","IMPRINT",EDGE,{"disambiguationData":[TD([[subQ2,-1.0]])],"derivedFrom":subQ1}),1.0]])]});}
            extrude(context, id + "F1", {"entities" : qUnion([Q0, Q1, Q2, Q3, Q4, Q5, Q6, Q7, Q8, Q9, Q10, Q11, Q12, Q13, Q14, Q15, Q16, Q17, Q18, Q19, Q20, Q21, Q22, Q23, Q24, Q25, Q26, Q27, Q28, Q29, Q30, Q31, Q32, Q33, Q34, Q35, Q36, Q37, Q38, Q39, Q40, Q41, Q42, Q43, Q44, Q45, Q46, Q47, Q48, Q49, Q50, Q51, Q52, Q53, Q54, Q55, Q56, Q57, Q58, Q59, Q60, Q61, Q62, Q63, Q64, Q65, Q66, Q67, Q68, Q69, Q70, Q71, Q72, Q73, Q74, Q75, Q76, Q77, Q78, Q79, Q80]), "depth" : 25 * mm, "offsetDistance" : 25 * mm});
        }
    });
